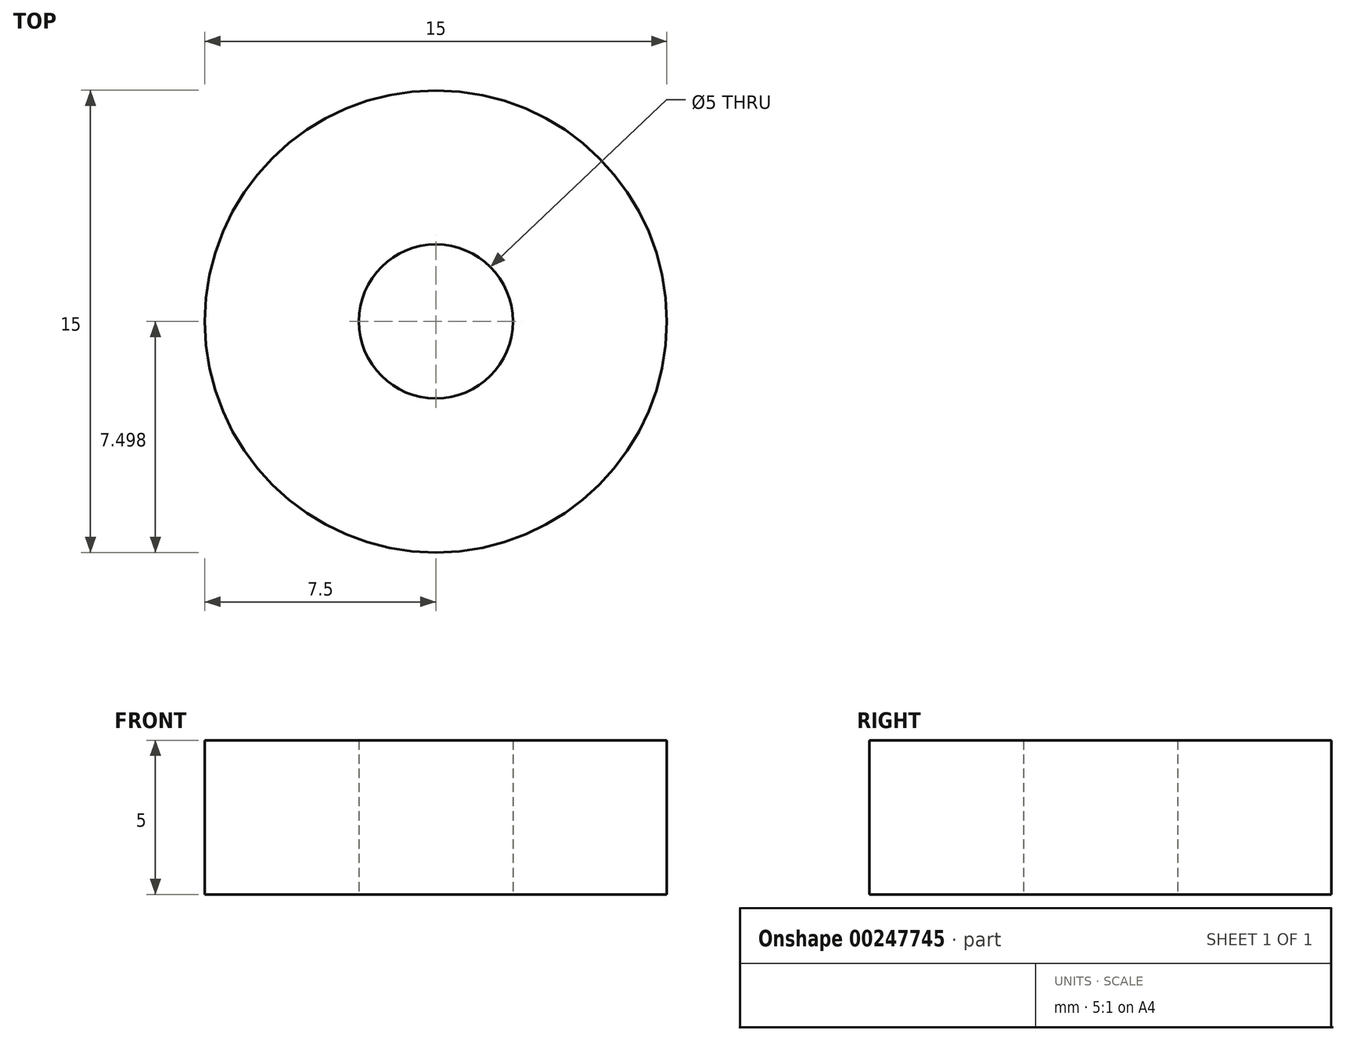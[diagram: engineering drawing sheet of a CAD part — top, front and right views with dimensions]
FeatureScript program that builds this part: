
annotation { "Feature Type Name" : "Feature", "Feature Type Description" : "" }
export const myFeature = defineFeature(function(context is Context, id is Id, definition is map)
    precondition{}
    {
        {
            var Q0;
            Q0=qCreatedBy(makeId("Top.planeOp"),FACE);
            var sketch = newSketch(context, id + "F0", { "sketchPlane" : qUnion([Q0])});
            skCircle(sketch, "E0", {"center": v(0, -2.53) * mm, "radius": 2.5 * mm});
            skCircle(sketch, "E1", {"center": v(0, -2.53) * mm, "radius": 7.5 * mm});
            skSolve(sketch);
        }
        {
            var Q0;
            Q0 = qSketchRegion(id + "F0", true);
            extrude(context, id + "F1", {"entities" : qUnion([Q0]), "depth" : 5 * mm});
        }
    });
